# Revit family: Gira_027228
name_source: partatom
category: Electrical Fixtures
revit_build: Autodesk Revit 2017 (Build: 20160225_1515(x64)
units: mm (PartAtom-declared; Revit-internal decimal feet)

## family parameters
Cut with Voids When Loaded = No
Host = Face
Maintain Annotation Orientation = No
Part Type = Normal
Room Calculation Point = No
Round Connector Dimension = Use Diameter
Shared = No

## types (1)
- Cov. sup.ring devices Ø 22.5 mm System 55 anthra.
    Available = No
    BIM (1) = https://media.stage.bim.site und Tasten.rfa?public/gira/36a6b08/Sys55_Abdeckung_Schalten und Tasten.rfa
    Category = Insert/cover for communication technology
    Data sheet (1) = https://katalog.gira.de
    Default Elevation = 1219 mm
    Description = Cov.sup.r.devices D22.5mm Sys55 AN,Cover plate with support ring for the insertion of command and signal devices (diameter  22.5 mm),,anthracite,Notes :,- For screw mounting only.,- For push buttons, slam buttons, key buttons, non-latching buttons, illuminated buttons, and mushroom buttons, selector switches, and signal lights, e.g. from Lumitas, Rafi, Elan, or Fanal.
    GTIN = 4010337272281
    HAN = 027228
    HeinzeBIM = https://bimportal.heinze.de
    Manufacturer = Gira
    Manufacturer URL = https://www.gira.de
    Name = Cov. sup.ring devices Ø 22.5 mm System 55 anthra.
    Transparent = No
    URL = http://katalog.gira.de

## geometry (parser evidence)
native form markers: Blend x2, Sweep x9
no freeform markers — native parametric forms only
